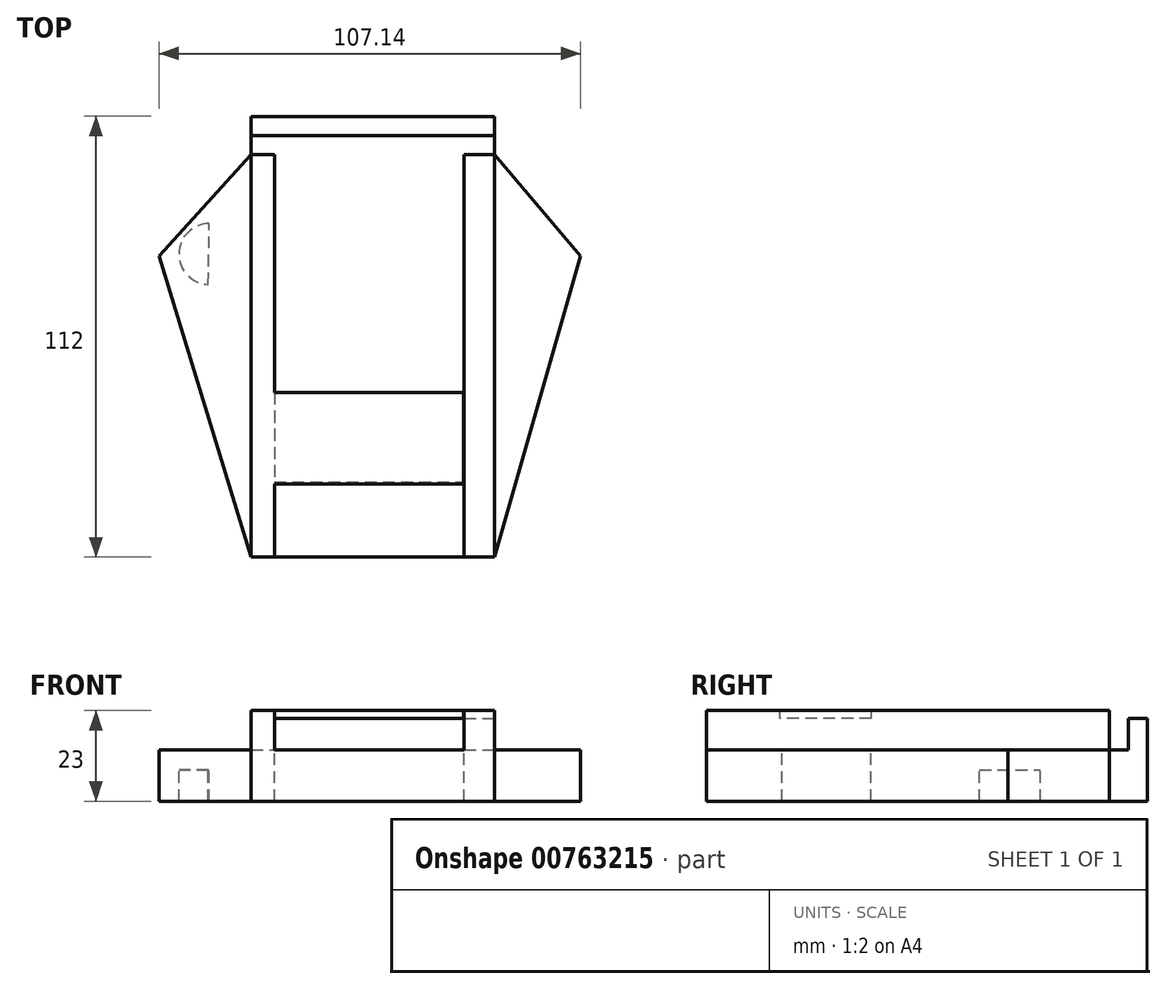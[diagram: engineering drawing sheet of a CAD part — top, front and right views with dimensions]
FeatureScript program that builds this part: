
annotation { "Feature Type Name" : "Feature", "Feature Type Description" : "" }
export const myFeature = defineFeature(function(context is Context, id is Id, definition is map)
    precondition{}
    {
        {
            var Q0;
            Q0=qCreatedBy(makeId("Top.planeOp"),FACE);
            var sketch = newSketch(context, id + "F0", { "sketchPlane" : qUnion([Q0])});
            skLineSegment(sketch, "E0.bottom", {"start": v(-30.91, 51.17) * mm, "end": v(30.91, 51.17) * mm});
            skLineSegment(sketch, "E0.top", {"start": v(-30.91, -51.17) * mm, "end": v(30.91, -51.17) * mm});
            skLineSegment(sketch, "E0.left", {"start": v(-30.91, 51.17) * mm, "end": v(-30.91, -51.17) * mm});
            skLineSegment(sketch, "E0.right", {"start": v(30.91, 51.17) * mm, "end": v(30.91, -51.17) * mm});
            skPoint(sketch, "E0.middle", {"position": v(0, 0) * mm});
            skLineSegment(sketch, "E1", {"start": v(-30.91, 51.17) * mm, "end": v(-54.37, 25.32) * mm});
            skLineSegment(sketch, "E2", {"start": v(-54.37, 25.32) * mm, "end": v(-30.91, -51.17) * mm});
            skLineSegment(sketch, "E3", {"start": v(30.91, 51.17) * mm, "end": v(52.77, 25.32) * mm});
            skLineSegment(sketch, "E4", {"start": v(52.77, 25.32) * mm, "end": v(30.91, -51.17) * mm});
            skSolve(sketch);
        }
        {
            var Q0;
            Q0 = qSketchRegion(id + "F0", true);
            extrude(context, id + "F1", {"entities" : qUnion([Q0]), "depth" : 5 * mm, "offsetDistance" : 25 * mm});
        }
        {
            var Q0;
            Q0=makeQuery(id+"F1.opExtrude","CAP_FACE",FACE,{"disambiguationData":[OSD([sQuery(id+"F0.wireOp",EDGE,"E0.bottom"),sQuery(id+"F0.wireOp",EDGE,"E0.top"),sQuery(id+"F0.wireOp",EDGE,"E1"),sQuery(id+"F0.wireOp",EDGE,"E2"),sQuery(id+"F0.wireOp",EDGE,"E3"),sQuery(id+"F0.wireOp",EDGE,"E4")])],"isStart":false});
            var sketch = newSketch(context, id + "F2", { "sketchPlane" : qUnion([Q0])});
            skLineSegment(sketch, "E5.bottom", {"start": v(-30.91, 51.17) * mm, "end": v(-25.05, 51.17) * mm});
            skLineSegment(sketch, "E5.top", {"start": v(-30.91, -51.17) * mm, "end": v(-25.05, -51.17) * mm});
            skLineSegment(sketch, "E5.left", {"start": v(-30.91, 51.17) * mm, "end": v(-30.91, -51.17) * mm});
            skLineSegment(sketch, "E5.right", {"start": v(-25.05, 51.17) * mm, "end": v(-25.05, -51.17) * mm});
            skLineSegment(sketch, "E6.bottom", {"start": v(30.91, 51.17) * mm, "end": v(23.19, 51.17) * mm});
            skLineSegment(sketch, "E6.top", {"start": v(30.91, -51.17) * mm, "end": v(23.19, -51.17) * mm});
            skLineSegment(sketch, "E6.left", {"start": v(30.91, 51.17) * mm, "end": v(30.91, -51.17) * mm});
            skLineSegment(sketch, "E6.right", {"start": v(23.19, 51.17) * mm, "end": v(23.19, -51.17) * mm});
            skSolve(sketch);
        }
        {
            var Q0;
            Q0 = qSketchRegion(id + "F2", true);
            var Q1;
            Q1=makeQuery(id+"F2.imprint","IMPRINT",FACE,{"disambiguationData":[TD([[makeQuery(id+"F2.imprint","IMPRINT",EDGE,{"derivedFrom":sQuery(id+"F2.wireOp",EDGE,"E5.bottom")}),-1.0]])]});
            extrude(context, id + "F3", {"entities" : qUnion([Q0, Q1]), "operationType" : NewBodyOperationType.ADD, "depth" : 10 * mm, "offsetDistance" : 25 * mm});
        }
        {
            var Q0;
            Q0=makeQuery(id+"F1.opExtrude","CAP_FACE",FACE,{"disambiguationData":[OSD([sQuery(id+"F0.wireOp",EDGE,"E0.bottom"),sQuery(id+"F0.wireOp",EDGE,"E0.top"),sQuery(id+"F0.wireOp",EDGE,"E1"),sQuery(id+"F0.wireOp",EDGE,"E2"),sQuery(id+"F0.wireOp",EDGE,"E3"),sQuery(id+"F0.wireOp",EDGE,"E4")])],"isStart":true});
            var sketch = newSketch(context, id + "F4", { "sketchPlane" : qUnion([Q0])});
            skLineSegment(sketch, "E7.bottom", {"start": v(-30.91, -51.17) * mm, "end": v(30.91, -51.17) * mm});
            skLineSegment(sketch, "E7.top", {"start": v(-30.91, -60.83) * mm, "end": v(30.91, -60.83) * mm});
            skLineSegment(sketch, "E7.left", {"start": v(-30.91, -51.17) * mm, "end": v(-30.91, -60.83) * mm});
            skLineSegment(sketch, "E7.right", {"start": v(30.91, -51.17) * mm, "end": v(30.91, -60.83) * mm});
            skSolve(sketch);
        }
        {
            var Q0;
            Q0=makeQuery(id+"F4.imprint","IMPRINT",FACE,{"disambiguationData":[TD([[makeQuery(id+"F4.imprint","IMPRINT",EDGE,{"derivedFrom":sQuery(id+"F4.wireOp",EDGE,"E7.bottom")}),-1.0]])]});
            extrude(context, id + "F5", {"entities" : qUnion([Q0]), "operationType" : NewBodyOperationType.ADD, "oppositeDirection" : true, "depth" : 5 * mm, "offsetDistance" : 25 * mm});
        }
        {
            var Q0;
            {var subQ0=sQuery(id+"F0.wireOp",EDGE,"E0.top");var subQ1=sQuery(id+"F0.wireOp",EDGE,"E0.bottom");Q0=makeQuery(id+"F5.boolean.opBoolean","MERGE",FACE,{"derivedFrom":[makeQuery(id+"F3.boolean.opBoolean","SPLIT",FACE,{"disambiguationData":[TD([makeQuery(id+"F3.opExtrude","SWEPT_FACE",FACE,{"disambiguationData":[OSD([sQuery(id+"F2.wireOp",EDGE,"E5.right")])]})])],"derivedFrom":makeQuery(id+"F1.opExtrude","CAP_FACE",FACE,{"disambiguationData":[OSD([subQ1,subQ0,sQuery(id+"F0.wireOp",EDGE,"E1"),sQuery(id+"F0.wireOp",EDGE,"E2"),sQuery(id+"F0.wireOp",EDGE,"E3"),sQuery(id+"F0.wireOp",EDGE,"E4")])],"isStart":false})}),makeQuery(id+"F5.opExtrude","CAP_FACE",FACE,{"disambiguationData":[OSD([sQuery(id+"F4.wireOp",EDGE,"E7.bottom"),sQuery(id+"F4.wireOp",EDGE,"E7.top"),sQuery(id+"F4.wireOp",EDGE,"E7.left"),sQuery(id+"F4.wireOp",EDGE,"E7.right")])],"isStart":false})]});}
            var sketch = newSketch(context, id + "F6", { "sketchPlane" : qUnion([Q0])});
            skLineSegment(sketch, "E8.bottom", {"start": v(-30.91, 60.83) * mm, "end": v(30.91, 60.83) * mm});
            skLineSegment(sketch, "E8.top", {"start": v(-30.91, 56) * mm, "end": v(30.91, 56) * mm});
            skLineSegment(sketch, "E8.left", {"start": v(-30.91, 60.83) * mm, "end": v(-30.91, 56) * mm});
            skLineSegment(sketch, "E8.right", {"start": v(30.91, 60.83) * mm, "end": v(30.91, 56) * mm});
            skSolve(sketch);
        }
        {
            var Q0;
            Q0 = qSketchRegion(id + "F6", true);
            extrude(context, id + "F7", {"entities" : qUnion([Q0]), "operationType" : NewBodyOperationType.ADD, "depth" : 8 * mm, "offsetDistance" : 25 * mm});
        }
        {
            var Q0;
            {var subQ0=sQuery(id+"F0.wireOp",EDGE,"E0.top");var subQ1=sQuery(id+"F0.wireOp",EDGE,"E0.bottom");Q0=makeQuery(id+"F5.boolean.opBoolean","MERGE",FACE,{"derivedFrom":[makeQuery(id+"F3.boolean.opBoolean","SPLIT",FACE,{"disambiguationData":[TD([makeQuery(id+"F3.opExtrude","SWEPT_FACE",FACE,{"disambiguationData":[OSD([sQuery(id+"F2.wireOp",EDGE,"E5.right")])]})])],"derivedFrom":makeQuery(id+"F1.opExtrude","CAP_FACE",FACE,{"disambiguationData":[OSD([subQ1,subQ0,sQuery(id+"F0.wireOp",EDGE,"E1"),sQuery(id+"F0.wireOp",EDGE,"E2"),sQuery(id+"F0.wireOp",EDGE,"E3"),sQuery(id+"F0.wireOp",EDGE,"E4")])],"isStart":false})}),makeQuery(id+"F5.opExtrude","CAP_FACE",FACE,{"disambiguationData":[OSD([sQuery(id+"F4.wireOp",EDGE,"E7.bottom"),sQuery(id+"F4.wireOp",EDGE,"E7.top"),sQuery(id+"F4.wireOp",EDGE,"E7.left"),sQuery(id+"F4.wireOp",EDGE,"E7.right")])],"isStart":false})]});}
            var sketch = newSketch(context, id + "F8", { "sketchPlane" : qUnion([Q0])});
            skLineSegment(sketch, "E9.bottom", {"start": v(-25.05, -32.08) * mm, "end": v(23.19, -32.08) * mm});
            skLineSegment(sketch, "E9.top", {"start": v(-25.05, -9.43) * mm, "end": v(23.19, -9.43) * mm});
            skLineSegment(sketch, "E9.left", {"start": v(-25.05, -32.08) * mm, "end": v(-25.05, -9.43) * mm});
            skLineSegment(sketch, "E9.right", {"start": v(23.19, -32.08) * mm, "end": v(23.19, -9.43) * mm});
            skSolve(sketch);
        }
        {
            var Q0;
            Q0 = qSketchRegion(id + "F8", true);
            extrude(context, id + "F9", {"entities" : qUnion([Q0]), "operationType" : NewBodyOperationType.REMOVE, "oppositeDirection" : true, "depth" : 5 * mm, "offsetDistance" : 25 * mm});
        }
        {
            var Q0;
            Q0=makeQuery(id+"F3.opExtrude","CAP_FACE",FACE,{"disambiguationData":[OSD([sQuery(id+"F2.wireOp",EDGE,"E5.bottom"),sQuery(id+"F2.wireOp",EDGE,"E5.top"),sQuery(id+"F2.wireOp",EDGE,"E5.left"),sQuery(id+"F2.wireOp",EDGE,"E5.right")])],"isStart":false});
            var sketch = newSketch(context, id + "F10", { "sketchPlane" : qUnion([Q0])});
            skLineSegment(sketch, "E10.bottom", {"start": v(-25.05, -9.32) * mm, "end": v(23.01, -9.32) * mm});
            skLineSegment(sketch, "E10.top", {"start": v(-25.05, -32.56) * mm, "end": v(23.01, -32.56) * mm});
            skLineSegment(sketch, "E10.left", {"start": v(-25.05, -9.32) * mm, "end": v(-25.05, -32.56) * mm});
            skLineSegment(sketch, "E10.right", {"start": v(23.01, -9.32) * mm, "end": v(23.01, -32.56) * mm});
            skSolve(sketch);
        }
        {
            var Q0;
            Q0 = qSketchRegion(id + "F10", true);
            extrude(context, id + "F11", {"entities" : qUnion([Q0]), "operationType" : NewBodyOperationType.ADD, "oppositeDirection" : true, "depth" : 2 * mm, "offsetDistance" : 25 * mm});
        }
        {
            var Q0;
            Q0=makeQuery(id+"F5.boolean.opBoolean","MERGE",FACE,{"derivedFrom":[makeQuery(id+"F1.opExtrude","CAP_FACE",FACE,{"disambiguationData":[OSD([sQuery(id+"F0.wireOp",EDGE,"E0.bottom"),sQuery(id+"F0.wireOp",EDGE,"E0.top"),sQuery(id+"F0.wireOp",EDGE,"E1"),sQuery(id+"F0.wireOp",EDGE,"E2"),sQuery(id+"F0.wireOp",EDGE,"E3"),sQuery(id+"F0.wireOp",EDGE,"E4")])],"isStart":true}),makeQuery(id+"F5.opExtrude","CAP_FACE",FACE,{"disambiguationData":[OSD([sQuery(id+"F4.wireOp",EDGE,"E7.bottom"),sQuery(id+"F4.wireOp",EDGE,"E7.top"),sQuery(id+"F4.wireOp",EDGE,"E7.left"),sQuery(id+"F4.wireOp",EDGE,"E7.right")])],"isStart":true})]});
            var sketch = newSketch(context, id + "F12", { "sketchPlane" : qUnion([Q0])});
            skArc(sketch, "E11", {"start": v(-41.57, -33.58) * mm, "mid": v(-49.3, -25.97) * mm, "end": v(-41.82, -18.13) * mm});
            skLineSegment(sketch, "E12", {"start": v(-41.82, -18.13) * mm, "end": v(-41.57, -33.58) * mm});
            skLineSegment(sketch, "E13.MirrorCS", {"start": v(41.82, -18.13) * mm, "end": v(41.57, -33.58) * mm});
            skArc(sketch, "E14.MirrorCS", {"start": v(41.57, -33.58) * mm, "mid": v(49.3, -25.97) * mm, "end": v(41.82, -18.13) * mm});
            skSolve(sketch);
        }
        {
            var Q0;
            Q0=makeQuery(id+"F12.imprint","IMPRINT",FACE,{"disambiguationData":[TD([[makeQuery(id+"F12.imprint","IMPRINT",EDGE,{"derivedFrom":sQuery(id+"F12.wireOp",EDGE,"E11")}),-1.0]])]});
            var Q1;
            Q1=makeQuery(id+"F12.imprint","IMPRINT",FACE,{"disambiguationData":[TD([[makeQuery(id+"F12.imprint","IMPRINT",EDGE,{"derivedFrom":sQuery(id+"F12.wireOp",EDGE,"E13.MirrorCS")}),1.0]])]});
            extrude(context, id + "F13", {"entities" : qUnion([Q0, Q1]), "operationType" : NewBodyOperationType.ADD, "depth" : 8 * mm, "offsetDistance" : 25 * mm});
        }
    });
